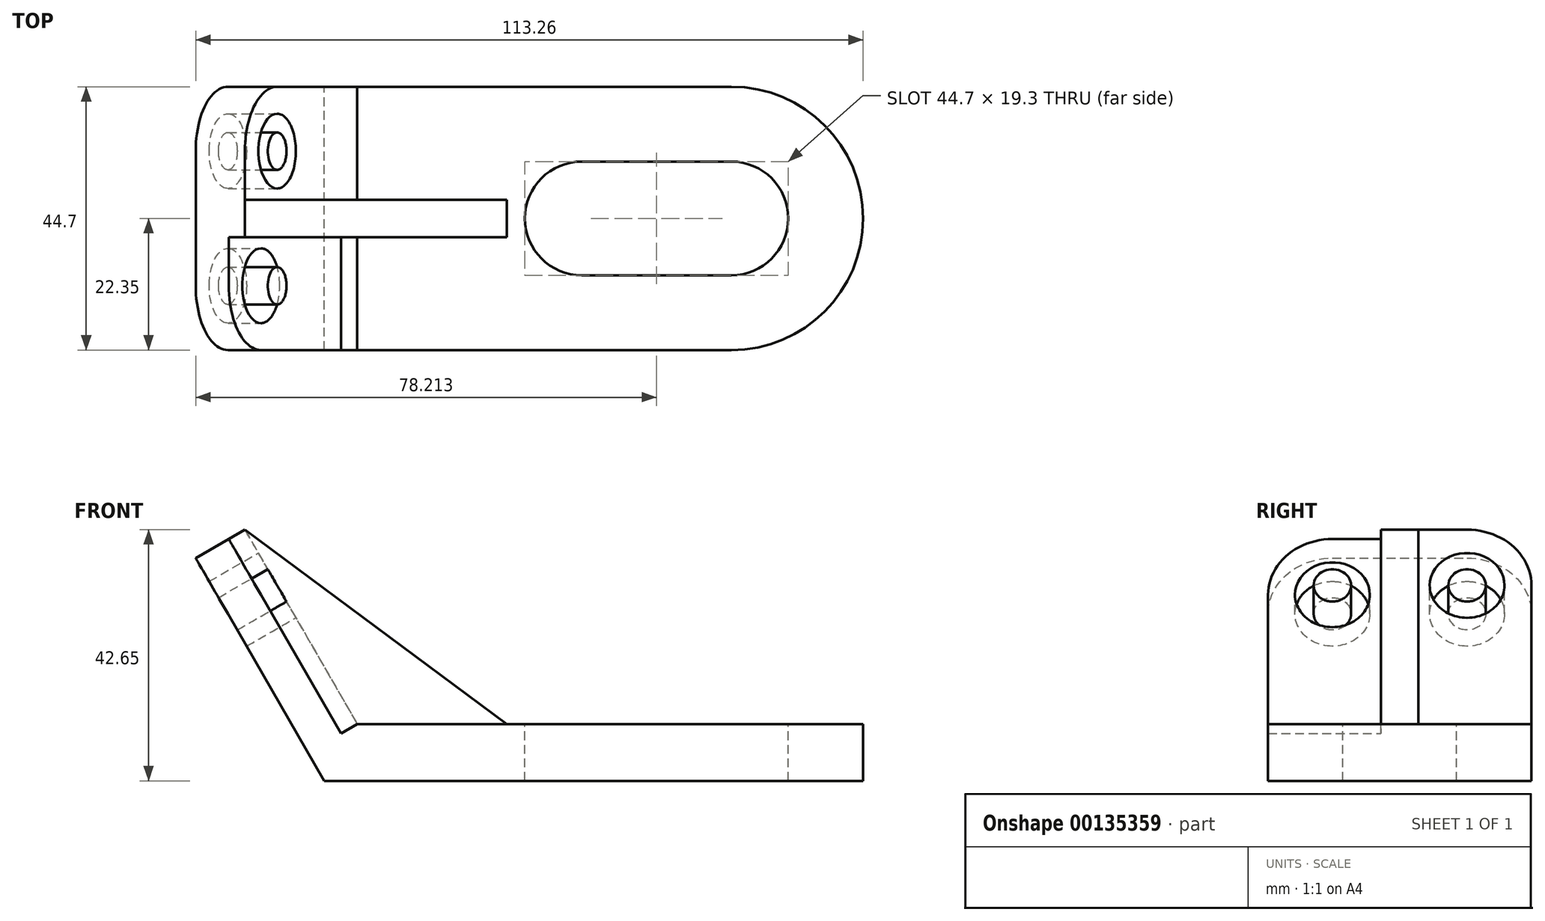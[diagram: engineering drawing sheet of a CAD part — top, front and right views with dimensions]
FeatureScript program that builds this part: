
annotation { "Feature Type Name" : "Feature", "Feature Type Description" : "" }
export const myFeature = defineFeature(function(context is Context, id is Id, definition is map)
    precondition{}
    {
        {
            var Q0;
            Q0=qCreatedBy(makeId("Front.planeOp"),FACE);
            var sketch = newSketch(context, id + "F0", { "sketchPlane" : qUnion([Q0])});
            skLineSegment(sketch, "E0", {"start": v(0, 0) * mm, "end": v(-21.84, 37.82) * mm});
            skLineSegment(sketch, "E1", {"start": v(-21.84, 37.82) * mm, "end": v(-13.48, 42.65) * mm});
            skLineSegment(sketch, "E2", {"start": v(-13.48, 42.65) * mm, "end": v(5.57, 9.65) * mm});
            skLineSegment(sketch, "E3", {"start": v(-13.48, 42.65) * mm, "end": v(30.97, 9.65) * mm});
            skLineSegment(sketch, "E4", {"start": v(5.57, 9.65) * mm, "end": v(91.42, 9.65) * mm});
            skLineSegment(sketch, "E5", {"start": v(0, 0) * mm, "end": v(91.42, 0) * mm});
            skLineSegment(sketch, "E6", {"start": v(91.42, 9.65) * mm, "end": v(91.42, 0) * mm});
            skSolve(sketch);
        }
        {
            var Q0;
            Q0=makeQuery(id+"F0.imprint","IMPRINT",FACE,{"disambiguationData":[TD([[makeQuery(id+"F0.imprint","IMPRINT",EDGE,{"derivedFrom":sQuery(id+"F0.wireOp",EDGE,"E0")}),-1.0]])]});
            extrude(context, id + "F1", {"entities" : qUnion([Q0]), "endBound" : BoundingType.SYMMETRIC, "depth" : 44.7 * mm});
        }
        {
            var Q0;
            {var subQ0=sQuery(id+"F0.wireOp",EDGE,"E2");Q0=makeQuery(id+"F0.imprint","IMPRINT",FACE,{"disambiguationData":[TD([[makeQuery(id+"F0.imprint","IMPRINT",EDGE,{"derivedFrom":subQ0}),1.0]])]});}
            extrude(context, id + "F2", {"entities" : qUnion([Q0]), "operationType" : NewBodyOperationType.ADD, "endBound" : BoundingType.SYMMETRIC, "depth" : 6.35 * mm});
        }
        {
            var Q0;
            Q0=makeQuery(id+"F1.opExtrude","CAP_EDGE",EDGE,{"disambiguationData":[OSD([sQuery(id+"F0.wireOp",EDGE,"E6")])],"isStart":true});
            var Q1;
            Q1=makeQuery(id+"F1.opExtrude","CAP_EDGE",EDGE,{"disambiguationData":[OSD([sQuery(id+"F0.wireOp",EDGE,"E6")])],"isStart":false});
            fillet(context, id + "F3", {"entities" : qUnion([Q0, Q1]), "radius" : 22.35 * mm, "tangentPropagation" : true, "allowEdgeOverflow" : false});
        }
        {
            var Q0;
            Q0=makeQuery(id+"F1.opExtrude","SWEPT_FACE",FACE,{"disambiguationData":[OSD([sQuery(id+"F0.wireOp",EDGE,"E4")])]});
            var sketch = newSketch(context, id + "F4", { "sketchPlane" : qUnion([Q0])});
            skLineSegment(sketch, "E7", {"start": v(43.67, 9.65) * mm, "end": v(69.07, 9.65) * mm});
            skLineSegment(sketch, "E8", {"start": v(69.07, -9.65) * mm, "end": v(43.67, -9.65) * mm});
            skArc(sketch, "E9", {"start": v(43.67, 9.65) * mm, "mid": v(34.02, 0) * mm, "end": v(43.67, -9.65) * mm});
            skArc(sketch, "E10", {"start": v(69.07, -9.65) * mm, "mid": v(78.72, 0) * mm, "end": v(69.07, 9.65) * mm});
            skSolve(sketch);
        }
        {
            var Q0;
            Q0 = qSketchRegion(id + "F4", true);
            extrude(context, id + "F5", {"entities" : qUnion([Q0]), "operationType" : NewBodyOperationType.REMOVE, "endBound" : BoundingType.UP_TO_NEXT, "oppositeDirection" : true, "depth" : 25.4 * mm});
        }
        {
            var Q0;
            Q0=makeQuery(id+"F1.opExtrude","SWEPT_FACE",FACE,{"disambiguationData":[OSD([sQuery(id+"F0.wireOp",EDGE,"E0")])]});
            var sketch = newSketch(context, id + "F6", { "sketchPlane" : qUnion([Q0])});
            skCircle(sketch, "E11", {"center": v(11.43, 32.75) * mm, "radius": 3.18 * mm});
            skCircle(sketch, "E12", {"center": v(-11.43, 32.75) * mm, "radius": 3.18 * mm});
            skCircle(sketch, "E13", {"center": v(11.43, 32.75) * mm, "radius": 6.35 * mm});
            skCircle(sketch, "E14", {"center": v(-11.43, 32.75) * mm, "radius": 6.35 * mm});
            skSolve(sketch);
        }
        {
            var Q0;
            {var subQ0=sQuery(id+"F0.wireOp",EDGE,"E4");var subQ1=sQuery(id+"F0.wireOp",EDGE,"E3");var subQ2=sQuery(id+"F0.wireOp",EDGE,"E2");Q0=makeQuery(id+"F2.boolean.opBoolean","SPLIT",FACE,{"disambiguationData":[TD([makeQuery(id+"F2.opExtrude","CAP_FACE",FACE,{"disambiguationData":[OSD([subQ2,subQ1,subQ0])],"isStart":false})])],"derivedFrom":makeQuery(id+"F1.opExtrude","SWEPT_FACE",FACE,{"disambiguationData":[OSD([subQ2])]})});}
            var sketch = newSketch(context, id + "F7", { "sketchPlane" : qUnion([Q0])});
            skCircle(sketch, "E15.0", {"center": v(-11.43, 32.75) * mm, "radius": 6.35 * mm});
            skCircle(sketch, "E15.1", {"center": v(-11.43, 32.75) * mm, "radius": 3.18 * mm});
            skCircle(sketch, "E16.0", {"center": v(11.43, 32.75) * mm, "radius": 6.35 * mm});
            skCircle(sketch, "E16.1", {"center": v(11.43, 32.75) * mm, "radius": 3.18 * mm});
            skSolve(sketch);
        }
        {
            var Q0;
            Q0=makeQuery(id+"F7.imprint","IMPRINT",FACE,{"disambiguationData":[TD([[makeQuery(id+"F7.imprint","IMPRINT",EDGE,{"derivedFrom":sQuery(id+"F7.wireOp",EDGE,"E16.1")}),-1.0]])]});
            var Q1;
            Q1=makeQuery(id+"F7.imprint","IMPRINT",FACE,{"disambiguationData":[TD([[makeQuery(id+"F7.imprint","IMPRINT",EDGE,{"derivedFrom":sQuery(id+"F7.wireOp",EDGE,"E15.1")}),-1.0]])]});
            extrude(context, id + "F8", {"entities" : qUnion([Q0, Q1]), "operationType" : NewBodyOperationType.REMOVE, "oppositeDirection" : true, "depth" : 25.4 * mm});
        }
        {
            var Q0;
            Q0=makeQuery(id+"F7.imprint","IMPRINT",FACE,{"disambiguationData":[TD([[makeQuery(id+"F7.imprint","IMPRINT",EDGE,{"derivedFrom":sQuery(id+"F7.wireOp",EDGE,"E15.0")}),-1.0]])]});
            var Q1;
            Q1=makeQuery(id+"F7.imprint","IMPRINT",FACE,{"disambiguationData":[TD([[makeQuery(id+"F7.imprint","IMPRINT",EDGE,{"derivedFrom":sQuery(id+"F7.wireOp",EDGE,"E16.0")}),-1.0]])]});
            extrude(context, id + "F9", {"entities" : qUnion([Q0, Q1]), "operationType" : NewBodyOperationType.REMOVE, "oppositeDirection" : true, "depth" : 3.17 * mm});
        }
        {
            var Q0;
            Q0=makeQuery(id+"F1.opExtrude","CAP_EDGE",EDGE,{"disambiguationData":[OSD([sQuery(id+"F0.wireOp",EDGE,"E1")])],"isStart":true});
            var Q1;
            Q1=makeQuery(id+"F1.opExtrude","CAP_EDGE",EDGE,{"disambiguationData":[OSD([sQuery(id+"F0.wireOp",EDGE,"E1")])],"isStart":false});
            fillet(context, id + "F10", {"entities" : qUnion([Q0, Q1]), "radius" : 10.92 * mm, "tangentPropagation" : true, "allowEdgeOverflow" : false});
        }
    });
